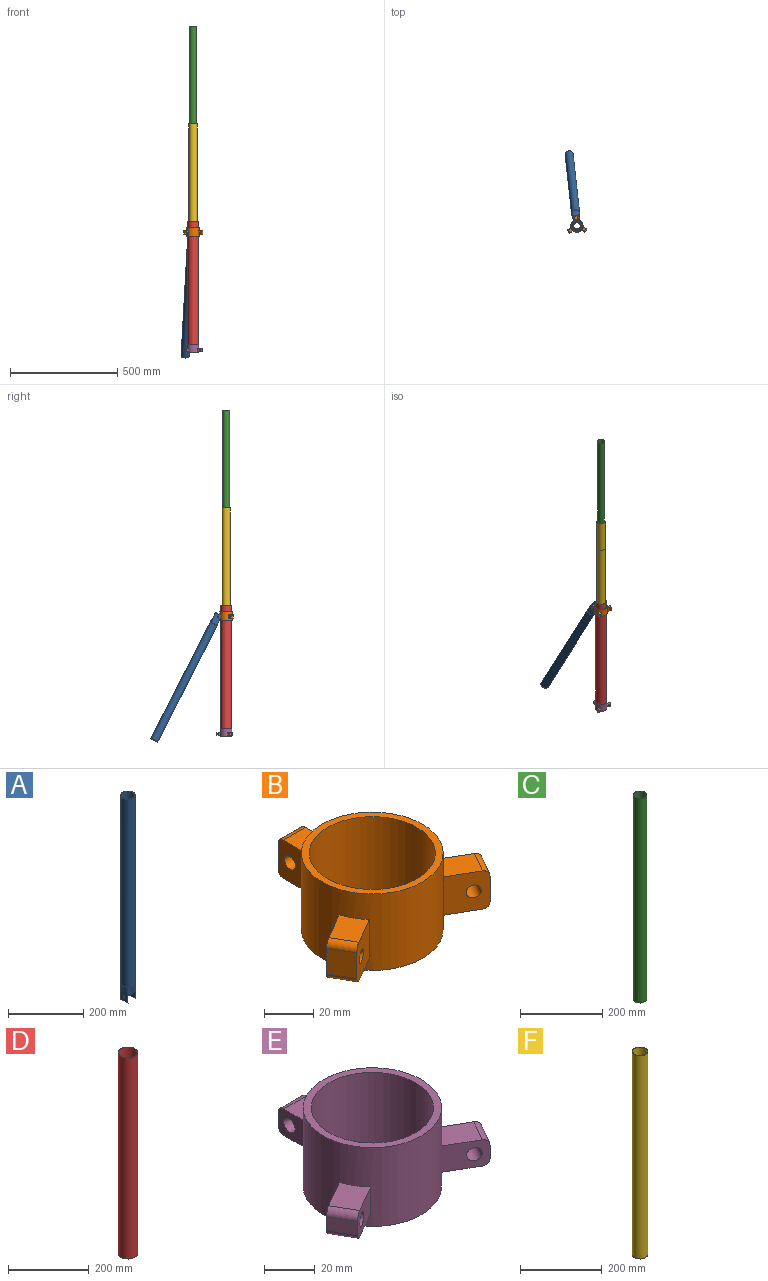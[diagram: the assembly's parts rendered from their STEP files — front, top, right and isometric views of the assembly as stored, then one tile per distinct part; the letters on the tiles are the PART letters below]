
ASSEMBLY  parts=6 mates=5
PART A: 13 faces, bbox 40.2x40.2x662.5 mm
  f0: bspline ~50.8x38.08mm, area 5140.8mm2, adj f2,f3,f4,f7,f8,f9,f10,f11
  f1: offset ~52.83x40.14mm, area 4678.3mm2, adj f2,f3,f6,f7,f8,f9,f10,f11
  f2: extruded ~22.09x14.39mm, area 293.5mm2, adj f0,f1,f3,f9,f11
  f3: plane 32.55x31.71mm, normal (0,0,-1), area 85.4mm2, adj f0,f1,f2,f8
  f4: cylinder r=19.05mm len=609.6mm, axis (0,0,-1), area 72965.9mm2, adj f0,f5
  f5: plane 38.1x38.1mm, normal (0,0,1), area 118.4mm2, adj f4,f6
  f6: cylinder r=18.03mm len=609.6mm, axis (0,0,-1), area 69074.4mm2, adj f1,f5
  f7: cylinder r=3.17mm len=3.86mm, axis (0,1,0), area 8.5mm2, adj f0,f1,f8,f10
  f8: extruded ~22.09x2.99mm, area 50.9mm2, adj f0,f1,f3,f7
  f9: cylinder r=3.17mm len=15.7mm, axis (0,1,0), area 19.1mm2, adj f0,f1,f2,f10
  f10: plane 22.86x1.64mm, normal (0,0,-1), area 23.3mm2, adj f0,f1,f7,f9
  f11: cylinder r=3.17mm len=6.35mm, axis (-1,0,0), area 21.5mm2, adj f0,f1,f2
  f12: cylinder r=3.17mm len=6.35mm, axis (-1,0,0), area 20.3mm2, adj f0,f1
PART B: 28 faces, bbox 89.3x77.3x38.1 mm
  f0: cylinder r=25.65mm len=51.31mm, axis (0,0,-1), area 6141.3mm2, adj f2,f3
  f1: cylinder r=28.83mm len=57.66mm, axis (0,0,-1), area 6169.6mm2, adj f2,f3,f4,f5,f6,f7,f16,f17
  f2: plane 57.66x57.66mm, normal (0,0,1), area 543.4mm2, adj f0,f1
  f3: plane 57.66x57.66mm, normal (0,0,-1), area 543.4mm2, adj f0,f1
  f4: plane 19.76x19.05mm, normal (1,0,0), area 340.4mm2, adj f1,f6,f7,f8,f9,f10,f11
  f5: plane 19.76x19.05mm, normal (-1,0,0), area 340.4mm2, adj f1,f6,f7,f8,f9,f10,f11
  f6: plane 16.58x12.7mm, normal (0,0,1), area 204.6mm2, adj f1,f4,f5,f10
  f7: plane 16.58x12.7mm, normal (0,0,-1), area 204.6mm2, adj f1,f4,f5,f8
  f8: cylinder r=3.17mm len=12.7mm, axis (-1,0,0), area 63.3mm2, adj f4,f5,f7,f9
  f9: plane 12.7x12.7mm, normal (0,1,0), area 161.3mm2, adj f4,f5,f8,f10
  f10: cylinder r=3.17mm len=12.7mm, axis (-1,0,0), area 63.3mm2, adj f4,f5,f6,f9
  f11: cylinder r=3.17mm len=12.7mm, axis (-1,0,0), area 253.4mm2, adj f4,f5
  f12: plane 12.7x11mm, normal (0.87,-0.5,0), area 161.3mm2, adj f14,f15,f18,f19
  f13: cylinder r=3.17mm len=14.17mm, axis (0.5,0.87,0), area 253.4mm2, adj f18,f19
  f14: cylinder r=3.17mm len=12.59mm, axis (0.5,0.87,0), area 63.3mm2, adj f12,f16,f18,f19
  f15: cylinder r=3.17mm len=12.59mm, axis (0.5,0.87,0), area 63.3mm2, adj f12,f17,f18,f19
  f16: plane 20.71x19.29mm, normal (0,0,1), area 204.6mm2, adj f1,f14,f18,f19
  f17: plane 20.71x19.29mm, normal (0,0,-1), area 204.6mm2, adj f1,f15,f18,f19
  f18: plane 19.05x17.11mm, normal (0.5,0.87,0), area 340.4mm2, adj f1,f12,f13,f14,f15,f16,f17
  f19: plane 19.05x17.11mm, normal (-0.5,-0.87,0), area 340.4mm2, adj f1,f12,f13,f14,f15,f16,f17
  f20: plane 19.05x17.11mm, normal (-0.5,0.87,0), area 340.4mm2, adj f1,f22,f23,f24,f25,f26,f27
  f21: plane 19.05x17.11mm, normal (0.5,-0.87,0), area 340.4mm2, adj f1,f22,f23,f24,f25,f26,f27
  f22: plane 20.71x19.29mm, normal (0,0,1), area 204.6mm2, adj f1,f20,f21,f26
  f23: plane 20.71x19.29mm, normal (0,0,-1), area 204.6mm2, adj f1,f20,f21,f24
  f24: cylinder r=3.17mm len=12.59mm, axis (0.5,-0.87,0), area 63.3mm2, adj f20,f21,f23,f25
  f25: plane 12.7x11mm, normal (-0.87,-0.5,0), area 161.3mm2, adj f20,f21,f24,f26
  f26: cylinder r=3.17mm len=12.59mm, axis (0.5,-0.87,0), area 63.3mm2, adj f20,f21,f22,f25
  f27: cylinder r=3.17mm len=14.17mm, axis (0.5,-0.87,0), area 253.4mm2, adj f20,f21
PART C: 4 faces, bbox 32.4x32.4x609.6 mm
  f0: cylinder r=15.18mm len=609.6mm, axis (0,0,-1), area 58129.5mm2, adj f2,f3
  f1: cylinder r=16.19mm len=609.6mm, axis (0,0,-1), area 62021mm2, adj f2,f3
  f2: plane 32.39x32.39mm, normal (0,0,1), area 100.1mm2, adj f0,f1
  f3: plane 32.39x32.39mm, normal (0,0,-1), area 100.1mm2, adj f0,f1
PART D: 4 faces, bbox 48.3x48.3x609.6 mm
  f0: cylinder r=23.11mm len=609.6mm, axis (0,0,-1), area 88531.9mm2, adj f2,f3
  f1: cylinder r=24.13mm len=609.6mm, axis (0,0,-1), area 92423.4mm2, adj f2,f3
  f2: plane 48.26x48.26mm, normal (0,0,1), area 150.8mm2, adj f0,f1
  f3: plane 48.26x48.26mm, normal (0,0,-1), area 150.8mm2, adj f0,f1
PART E: 28 faces, bbox 86.6x75x38.1 mm
  f0: cylinder r=24.13mm len=48.26mm, axis (0,0,-1), area 5776.5mm2, adj f2,f3
  f1: cylinder r=27.3mm len=54.61mm, axis (0,0,-1), area 6048.2mm2, adj f2,f3,f4,f5,f6,f7,f16,f17
  f2: plane 54.61x54.61mm, normal (0,0,1), area 513mm2, adj f0,f1
  f3: plane 54.61x54.61mm, normal (0,0,-1), area 513mm2, adj f0,f1
  f4: plane 19.8x12.7mm, normal (1,0,0), area 215.4mm2, adj f1,f6,f7,f8,f9,f10,f11
  f5: plane 19.8x12.7mm, normal (-1,0,0), area 215.4mm2, adj f1,f6,f7,f8,f9,f10,f11
  f6: plane 16.62x12.7mm, normal (0,0,1), area 204.8mm2, adj f1,f4,f5,f10
  f7: plane 16.62x12.7mm, normal (0,0,-1), area 204.8mm2, adj f1,f4,f5,f8
  f8: cylinder r=3.17mm len=12.7mm, axis (-1,0,0), area 63.3mm2, adj f4,f5,f7,f9
  f9: plane 12.7x6.35mm, normal (0,1,0), area 80.6mm2, adj f4,f5,f8,f10
  f10: cylinder r=3.17mm len=12.7mm, axis (-1,0,0), area 63.3mm2, adj f4,f5,f6,f9
  f11: cylinder r=3.17mm len=12.7mm, axis (-1,0,0), area 253.4mm2, adj f4,f5
  f12: plane 11x6.35mm, normal (-0.87,-0.5,0), area 80.6mm2, adj f14,f15,f18,f19
  f13: cylinder r=3.17mm len=14.17mm, axis (0.5,-0.87,0), area 253.4mm2, adj f18,f19
  f14: cylinder r=3.17mm len=12.59mm, axis (0.5,-0.87,0), area 63.3mm2, adj f12,f16,f18,f19
  f15: cylinder r=3.17mm len=12.59mm, axis (0.5,-0.87,0), area 63.3mm2, adj f12,f17,f18,f19
  f16: plane 20.75x19.31mm, normal (0,0,1), area 204.8mm2, adj f1,f14,f18,f19
  f17: plane 20.75x19.31mm, normal (0,0,-1), area 204.8mm2, adj f1,f15,f18,f19
  f18: plane 17.15x12.7mm, normal (0.5,-0.87,0), area 215.4mm2, adj f1,f12,f13,f14,f15,f16,f17
  f19: plane 17.15x12.7mm, normal (-0.5,0.87,0), area 215.4mm2, adj f1,f12,f13,f14,f15,f16,f17
  f20: plane 17.15x12.7mm, normal (-0.5,-0.87,0), area 215.4mm2, adj f1,f22,f23,f24,f25,f26,f27
  f21: plane 17.15x12.7mm, normal (0.5,0.87,0), area 215.4mm2, adj f1,f22,f23,f24,f25,f26,f27
  f22: plane 20.75x19.31mm, normal (0,0,1), area 204.8mm2, adj f1,f20,f21,f26
  f23: plane 20.75x19.31mm, normal (0,0,-1), area 204.8mm2, adj f1,f20,f21,f24
  f24: cylinder r=3.17mm len=12.59mm, axis (0.5,0.87,0), area 63.3mm2, adj f20,f21,f23,f25
  f25: plane 11x6.35mm, normal (0.87,-0.5,0), area 80.6mm2, adj f20,f21,f24,f26
  f26: cylinder r=3.17mm len=12.59mm, axis (0.5,0.87,0), area 63.3mm2, adj f20,f21,f22,f25
  f27: cylinder r=3.17mm len=14.17mm, axis (0.5,0.87,0), area 253.4mm2, adj f20,f21
PART F: 4 faces, bbox 38.1x38.1x609.6 mm
  f0: cylinder r=18.03mm len=609.6mm, axis (0,0,-1), area 69074.4mm2, adj f2,f3
  f1: cylinder r=19.05mm len=609.6mm, axis (0,0,-1), area 72965.9mm2, adj f2,f3
  f2: plane 38.1x38.1mm, normal (0,0,1), area 118.4mm2, adj f0,f1
  f3: plane 38.1x38.1mm, normal (0,0,-1), area 118.4mm2, adj f0,f1
PLACE A rot(axis=(0.05,-0.97,-0.23),178.5deg) t=(-6.32,58.05,525.88)mm
PLACE B rot(axis=(0,0,-1),113.8deg) t=(0,0,543.9)mm
PLACE C rot(axis=(0,0,1),158.8deg) t=(0,0,914.4)mm
PLACE D at identity fixed
PLACE E at identity
PLACE F rot(axis=(0,0,1),0deg) t=(0,0,457.2)mm
MATE cylindrical F.f1 <-> D.f1  axis (0,0,-1) through (0,0,457.2)mm
MATE revolute B.f27 <-> A.f11  axis (-0.99,-0.11,0) through (-4.44,40.76,559.77)mm
MATE cylindrical D.f1 <-> B.f0  axis (0,0,-1) through (0,0,609.6)mm
MATE cylindrical E.f1 <-> D.f0  axis (0,0,-1) through (0,0,0)mm
MATE cylindrical F.f1 <-> C.f1  axis (0,0,1) through (0,0,1066.8)mm
